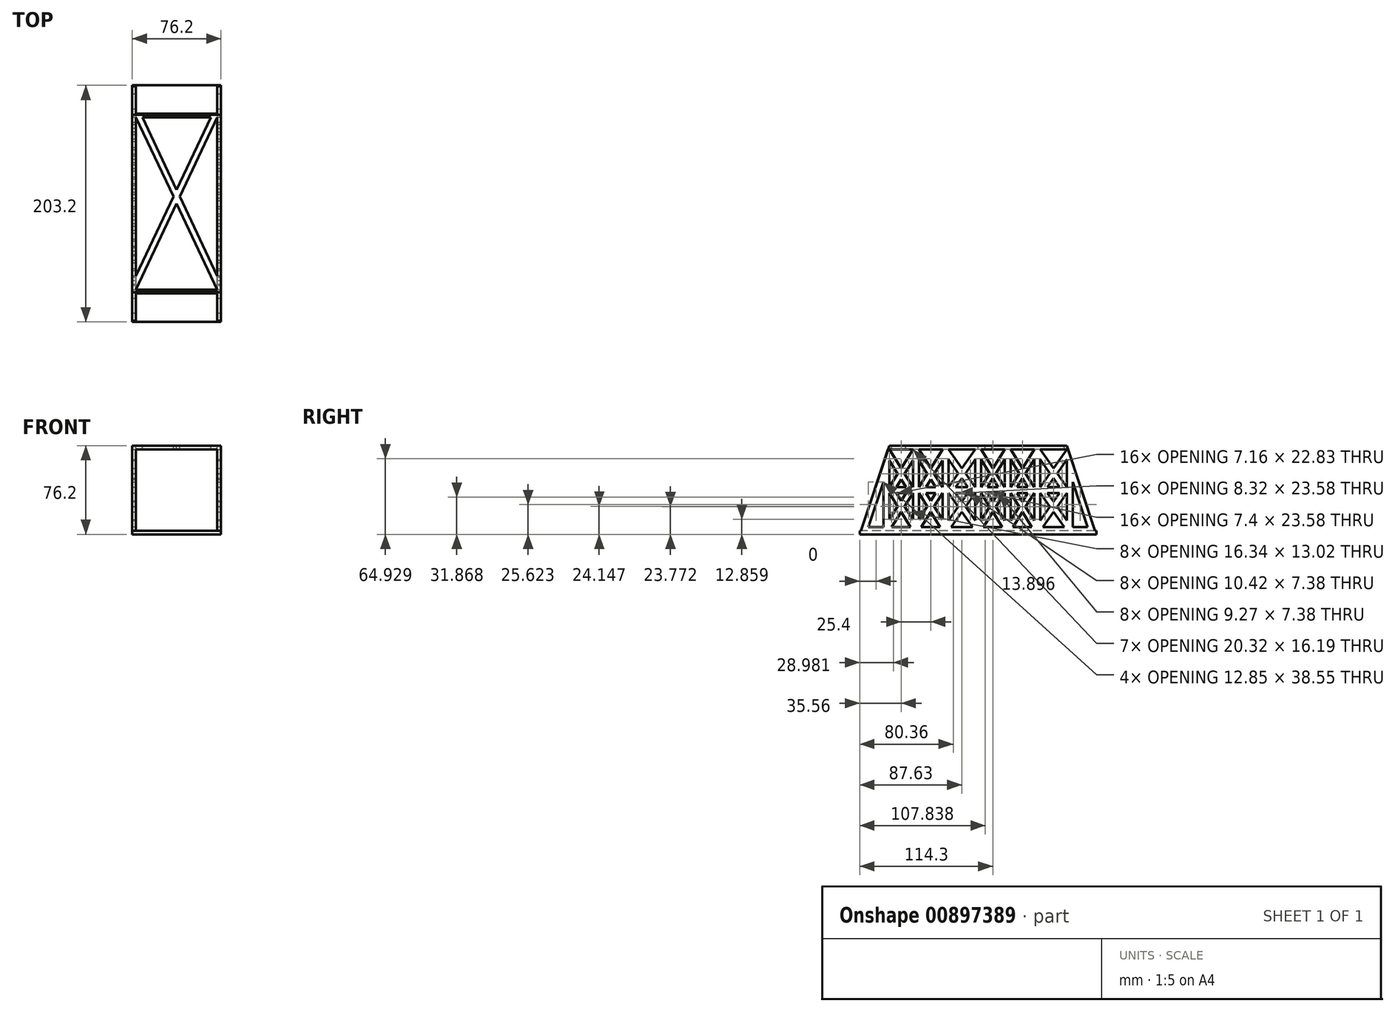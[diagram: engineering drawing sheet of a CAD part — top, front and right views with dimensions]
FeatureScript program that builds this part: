
annotation { "Feature Type Name" : "Feature", "Feature Type Description" : "" }
export const myFeature = defineFeature(function(context is Context, id is Id, definition is map)
    precondition{}
    {
        {
            var Q0;
            Q0=qCreatedBy(makeId("Right.planeOp"),FACE);
            var sketch = newSketch(context, id + "F0", { "sketchPlane" : qUnion([Q0])});
            skLineSegment(sketch, "E0", {"start": v(-101.6, -38.1) * mm, "end": v(101.6, -38.1) * mm});
            skLineSegment(sketch, "E1", {"start": v(-76.2, 38.1) * mm, "end": v(76.2, 38.1) * mm});
            skLineSegment(sketch, "E2", {"start": v(-76.2, 38.1) * mm, "end": v(-101.6, -38.1) * mm});
            skLineSegment(sketch, "E3", {"start": v(76.2, 38.1) * mm, "end": v(101.6, -38.1) * mm});
            skSolve(sketch);
        }
        {
            var Q0;
            Q0 = qSketchRegion(id + "F0", true);
            extrude(context, id + "F1", {"entities" : qUnion([Q0]), "endBound" : BoundingType.SYMMETRIC, "depth" : 76.2 * mm, "offsetDistance" : 25.4 * mm});
        }
        {
            var Q0;
            Q0=makeQuery(id+"F1.opExtrude","CAP_FACE",FACE,{"disambiguationData":[OSD([sQuery(id+"F0.wireOp",EDGE,"E0"),sQuery(id+"F0.wireOp",EDGE,"E1"),sQuery(id+"F0.wireOp",EDGE,"E2"),sQuery(id+"F0.wireOp",EDGE,"E3")])],"isStart":false});
            var sketch = newSketch(context, id + "F2", { "sketchPlane" : qUnion([Q0])});
            skLineSegment(sketch, "E4.bottom", {"start": v(76.2, -34.93) * mm, "end": v(-76.2, -34.93) * mm});
            skLineSegment(sketch, "E4.top", {"start": v(76.2, 34.93) * mm, "end": v(-76.2, 34.93) * mm});
            skLineSegment(sketch, "E4.left", {"start": v(76.2, -34.93) * mm, "end": v(76.2, 34.93) * mm});
            skLineSegment(sketch, "E4.right", {"start": v(-76.2, -34.93) * mm, "end": v(-76.2, 34.93) * mm});
            skPoint(sketch, "E4.middle", {"position": v(0, 0) * mm});
            skLineSegment(sketch, "E5.bottom", {"start": v(76.2, -2.54) * mm, "end": v(-76.2, -2.54) * mm});
            skLineSegment(sketch, "E5.top", {"start": v(76.2, 2.54) * mm, "end": v(-76.2, 2.54) * mm});
            skLineSegment(sketch, "E5.left", {"start": v(76.2, -2.54) * mm, "end": v(76.2, 2.54) * mm});
            skLineSegment(sketch, "E5.right", {"start": v(-76.2, -2.54) * mm, "end": v(-76.2, 2.54) * mm});
            skLineSegment(sketch, "E6.bottom", {"start": v(-50.8, -34.93) * mm, "end": v(-55.88, -34.93) * mm});
            skLineSegment(sketch, "E6.top", {"start": v(-50.8, 34.93) * mm, "end": v(-55.88, 34.93) * mm});
            skLineSegment(sketch, "E6.left", {"start": v(-50.8, -34.92) * mm, "end": v(-50.8, 34.93) * mm});
            skLineSegment(sketch, "E6.right", {"start": v(-55.88, -34.92) * mm, "end": v(-55.88, 34.93) * mm});
            skPoint(sketch, "E6.middle", {"position": v(-53.34, 0) * mm});
            skLineSegment(sketch, "E7.bottom", {"start": v(-25.4, -34.93) * mm, "end": v(-30.48, -34.93) * mm});
            skLineSegment(sketch, "E7.top", {"start": v(-25.4, 34.93) * mm, "end": v(-30.48, 34.93) * mm});
            skLineSegment(sketch, "E7.left", {"start": v(-25.4, -34.93) * mm, "end": v(-25.4, 34.93) * mm});
            skLineSegment(sketch, "E7.right", {"start": v(-30.48, -34.93) * mm, "end": v(-30.48, 34.93) * mm});
            skPoint(sketch, "E7.middle", {"position": v(-27.94, 0) * mm});
            skLineSegment(sketch, "E8.bottom", {"start": v(27.94, -34.93) * mm, "end": v(22.86, -34.93) * mm});
            skLineSegment(sketch, "E8.top", {"start": v(27.94, 34.93) * mm, "end": v(22.86, 34.93) * mm});
            skLineSegment(sketch, "E8.left", {"start": v(27.94, -34.92) * mm, "end": v(27.94, 34.93) * mm});
            skLineSegment(sketch, "E8.right", {"start": v(22.86, -34.93) * mm, "end": v(22.86, 34.93) * mm});
            skPoint(sketch, "E8.middle", {"position": v(25.4, 0) * mm});
            skLineSegment(sketch, "E9.bottom", {"start": v(53.34, -34.93) * mm, "end": v(48.26, -34.93) * mm});
            skLineSegment(sketch, "E9.top", {"start": v(53.34, 34.93) * mm, "end": v(48.26, 34.93) * mm});
            skLineSegment(sketch, "E9.left", {"start": v(53.34, -34.93) * mm, "end": v(53.34, 34.93) * mm});
            skLineSegment(sketch, "E9.right", {"start": v(48.26, -34.93) * mm, "end": v(48.26, 34.93) * mm});
            skPoint(sketch, "E9.middle", {"position": v(50.8, 0) * mm});
            skLineSegment(sketch, "E10.bottom", {"start": v(2.54, -34.93) * mm, "end": v(-2.54, -34.93) * mm});
            skLineSegment(sketch, "E10.top", {"start": v(2.54, 34.93) * mm, "end": v(-2.54, 34.93) * mm});
            skLineSegment(sketch, "E10.left", {"start": v(2.54, -34.93) * mm, "end": v(2.54, 34.93) * mm});
            skLineSegment(sketch, "E10.right", {"start": v(-2.54, -34.93) * mm, "end": v(-2.54, 34.93) * mm});
            skLineSegment(sketch, "E11", {"start": v(-76.2, 34.93) * mm, "end": v(-55.88, 2.54) * mm});
            skLineSegment(sketch, "E12", {"start": v(-55.88, 34.93) * mm, "end": v(-76.2, 2.54) * mm});
            skLineSegment(sketch, "E13", {"start": v(-50.8, 34.93) * mm, "end": v(-30.48, 2.54) * mm});
            skLineSegment(sketch, "E14", {"start": v(-2.54, 34.92) * mm, "end": v(-25.4, 2.54) * mm});
            skLineSegment(sketch, "E15", {"start": v(-76.2, -2.54) * mm, "end": v(-55.88, -34.93) * mm});
            skLineSegment(sketch, "E16", {"start": v(-55.88, -2.54) * mm, "end": v(-76.2, -34.93) * mm});
            skLineSegment(sketch, "E17", {"start": v(-50.8, -2.54) * mm, "end": v(-30.48, -34.92) * mm});
            skLineSegment(sketch, "E18", {"start": v(-30.48, -2.54) * mm, "end": v(-50.8, -34.92) * mm});
            skLineSegment(sketch, "E19", {"start": v(-25.4, -2.54) * mm, "end": v(-2.54, -34.92) * mm});
            skLineSegment(sketch, "E20", {"start": v(-2.54, -2.54) * mm, "end": v(-25.4, -34.93) * mm});
            skLineSegment(sketch, "E21", {"start": v(-55.88, 25.37) * mm, "end": v(-70.2, 2.54) * mm});
            skLineSegment(sketch, "E22", {"start": v(-70.2, -2.54) * mm, "end": v(-55.88, -25.37) * mm});
            skLineSegment(sketch, "E23", {"start": v(-61.88, -2.54) * mm, "end": v(-76.2, -25.37) * mm});
            skLineSegment(sketch, "E24", {"start": v(-44.8, -2.54) * mm, "end": v(-30.48, -25.37) * mm});
            skLineSegment(sketch, "E25", {"start": v(-36.48, -2.54) * mm, "end": v(-50.8, -25.37) * mm});
            skLineSegment(sketch, "E26", {"start": v(-19.18, -2.54) * mm, "end": v(-2.54, -26.12) * mm});
            skLineSegment(sketch, "E27", {"start": v(-8.76, -2.54) * mm, "end": v(-25.4, -26.12) * mm});
            skLineSegment(sketch, "E28", {"start": v(-25.4, 34.93) * mm, "end": v(-2.54, 2.54) * mm});
            skLineSegment(sketch, "E29", {"start": v(-25.4, 26.12) * mm, "end": v(-8.76, 2.54) * mm});
            skLineSegment(sketch, "E30", {"start": v(-2.54, 26.12) * mm, "end": v(-19.18, 2.54) * mm});
            skLineSegment(sketch, "E31", {"start": v(-30.48, 34.92) * mm, "end": v(-50.8, 2.54) * mm});
            skLineSegment(sketch, "E32", {"start": v(-50.8, 25.37) * mm, "end": v(-36.48, 2.54) * mm});
            skLineSegment(sketch, "E33", {"start": v(-30.48, 25.37) * mm, "end": v(-44.8, 2.54) * mm});
            skLineSegment(sketch, "E34", {"start": v(-76.2, 25.37) * mm, "end": v(-61.88, 2.54) * mm});
            skLineSegment(sketch, "E35", {"start": v(2.54, 34.92) * mm, "end": v(22.86, 2.54) * mm});
            skLineSegment(sketch, "E36", {"start": v(22.86, 34.92) * mm, "end": v(2.54, 2.54) * mm});
            skLineSegment(sketch, "E37", {"start": v(2.54, 26.12) * mm, "end": v(17.33, 2.54) * mm});
            skLineSegment(sketch, "E38", {"start": v(22.86, 26.12) * mm, "end": v(8.07, 2.54) * mm});
            skLineSegment(sketch, "E39", {"start": v(27.94, 34.92) * mm, "end": v(48.26, 2.54) * mm});
            skLineSegment(sketch, "E40", {"start": v(27.94, 2.54) * mm, "end": v(48.26, 34.92) * mm});
            skLineSegment(sketch, "E41", {"start": v(53.34, 34.93) * mm, "end": v(76.2, 2.54) * mm});
            skLineSegment(sketch, "E42", {"start": v(53.34, 2.54) * mm, "end": v(76.2, 34.93) * mm});
            skLineSegment(sketch, "E43", {"start": v(53.34, -2.54) * mm, "end": v(76.2, -34.93) * mm});
            skLineSegment(sketch, "E44", {"start": v(53.34, -34.93) * mm, "end": v(76.2, -2.54) * mm});
            skLineSegment(sketch, "E45", {"start": v(48.26, -34.92) * mm, "end": v(27.94, -2.54) * mm});
            skLineSegment(sketch, "E46", {"start": v(48.26, -2.54) * mm, "end": v(27.94, -34.92) * mm});
            skLineSegment(sketch, "E47", {"start": v(2.54, -2.54) * mm, "end": v(22.86, -34.92) * mm});
            skLineSegment(sketch, "E48", {"start": v(22.86, -2.54) * mm, "end": v(2.54, -34.92) * mm});
            skLineSegment(sketch, "E49", {"start": v(27.94, 26.12) * mm, "end": v(42.73, 2.54) * mm});
            skLineSegment(sketch, "E50", {"start": v(48.26, 26.12) * mm, "end": v(33.47, 2.54) * mm});
            skLineSegment(sketch, "E51", {"start": v(53.34, 26.12) * mm, "end": v(69.98, 2.54) * mm});
            skLineSegment(sketch, "E52", {"start": v(76.2, 26.12) * mm, "end": v(59.56, 2.54) * mm});
            skLineSegment(sketch, "E53", {"start": v(59.56, -2.54) * mm, "end": v(76.2, -26.12) * mm});
            skLineSegment(sketch, "E54", {"start": v(69.98, -2.54) * mm, "end": v(53.34, -26.12) * mm});
            skLineSegment(sketch, "E55", {"start": v(48.26, -26.12) * mm, "end": v(33.47, -2.54) * mm});
            skLineSegment(sketch, "E56", {"start": v(42.73, -2.54) * mm, "end": v(27.94, -26.12) * mm});
            skLineSegment(sketch, "E57", {"start": v(22.86, -26.12) * mm, "end": v(8.07, -2.54) * mm});
            skLineSegment(sketch, "E58", {"start": v(17.33, -2.54) * mm, "end": v(2.54, -26.12) * mm});
            skLineSegment(sketch, "E59", {"start": v(-81.28, -34.93) * mm, "end": v(-81.28, 6.8) * mm});
            skLineSegment(sketch, "E60", {"start": v(-81.28, 6.8) * mm, "end": v(-95.19, -34.93) * mm});
            skLineSegment(sketch, "E61", {"start": v(-95.19, -34.92) * mm, "end": v(-81.28, -34.93) * mm});
            skLineSegment(sketch, "E62.MirrorCS", {"start": v(81.28, 6.8) * mm, "end": v(95.19, -34.93) * mm});
            skLineSegment(sketch, "E63.MirrorCS", {"start": v(81.28, -34.93) * mm, "end": v(81.28, 6.8) * mm});
            skLineSegment(sketch, "E64.MirrorCS", {"start": v(95.19, -34.92) * mm, "end": v(81.28, -34.93) * mm});
            skSolve(sketch);
        }
        {
            var Q0;
            Q0=makeQuery(id+"F2.imprint","IMPRINT",FACE,{"disambiguationData":[TD([[makeQuery(id+"F2.imprint","IMPRINT",EDGE,{"derivedFrom":sQuery(id+"F2.wireOp",EDGE,"E59")}),1.0]])]});
            var Q1;
            {var subQ0=sQuery(id+"F2.wireOp",EDGE,"E16");var subQ3=sQuery(id+"F2.wireOp",EDGE,"E15");var subQ5=makeQuery(id+"F2.imprint","INTERSECT",VERTEX,{"derivedFrom":[subQ3,subQ0]});Q1=makeQuery(id+"F2.imprint","IMPRINT",FACE,{"disambiguationData":[TD([[makeQuery(id+"F2.imprint","IMPRINT",EDGE,{"disambiguationData":[TD([[subQ5,-1.0]])],"derivedFrom":subQ0}),1.0]])]});}
            var Q2;
            {var subQ1=sQuery(id+"F2.wireOp",EDGE,"E4.right");var subQ3=sQuery(id+"F2.wireOp",EDGE,"E23");var subQ4=makeQuery(id+"F2.imprint","INTERSECT",VERTEX,{"derivedFrom":[subQ1,subQ3]});Q2=makeQuery(id+"F2.imprint","IMPRINT",FACE,{"disambiguationData":[TD([[makeQuery(id+"F2.imprint","IMPRINT",EDGE,{"disambiguationData":[TD([[subQ4,1.0]])],"derivedFrom":subQ3}),-1.0]])]});}
            var Q3;
            {var subQ0=sQuery(id+"F2.wireOp",EDGE,"E22");var subQ1=sQuery(id+"F2.wireOp",EDGE,"E5.bottom");var subQ2=makeQuery(id+"F2.imprint","INTERSECT",VERTEX,{"derivedFrom":[subQ1,subQ0]});Q3=makeQuery(id+"F2.imprint","IMPRINT",FACE,{"disambiguationData":[TD([[makeQuery(id+"F2.imprint","IMPRINT",EDGE,{"disambiguationData":[TD([[subQ2,1.0]])],"derivedFrom":subQ1}),1.0]])]});}
            var Q4;
            {var subQ1=sQuery(id+"F2.wireOp",EDGE,"E6.right");var subQ3=sQuery(id+"F2.wireOp",EDGE,"E22");var subQ4=makeQuery(id+"F2.imprint","INTERSECT",VERTEX,{"derivedFrom":[subQ1,subQ3]});Q4=makeQuery(id+"F2.imprint","IMPRINT",FACE,{"disambiguationData":[TD([[makeQuery(id+"F2.imprint","IMPRINT",EDGE,{"disambiguationData":[TD([[subQ4,1.0]])],"derivedFrom":subQ3}),1.0]])]});}
            var Q5;
            {var subQ0=sQuery(id+"F2.wireOp",EDGE,"E21");var subQ1=sQuery(id+"F2.wireOp",EDGE,"E5.top");var subQ2=makeQuery(id+"F2.imprint","INTERSECT",VERTEX,{"derivedFrom":[subQ1,subQ0]});Q5=makeQuery(id+"F2.imprint","IMPRINT",FACE,{"disambiguationData":[TD([[makeQuery(id+"F2.imprint","IMPRINT",EDGE,{"disambiguationData":[TD([[subQ2,1.0]])],"derivedFrom":subQ1}),-1.0]])]});}
            var Q6;
            {var subQ0=sQuery(id+"F2.wireOp",EDGE,"E11");var subQ3=sQuery(id+"F2.wireOp",EDGE,"E12");var subQ5=makeQuery(id+"F2.imprint","INTERSECT",VERTEX,{"derivedFrom":[subQ0,subQ3]});Q6=makeQuery(id+"F2.imprint","IMPRINT",FACE,{"disambiguationData":[TD([[makeQuery(id+"F2.imprint","IMPRINT",EDGE,{"disambiguationData":[TD([[subQ5,1.0]])],"derivedFrom":subQ0}),1.0]])]});}
            var Q7;
            {var subQ1=sQuery(id+"F2.wireOp",EDGE,"E4.right");var subQ3=sQuery(id+"F2.wireOp",EDGE,"E34");var subQ4=makeQuery(id+"F2.imprint","INTERSECT",VERTEX,{"derivedFrom":[subQ1,subQ3]});Q7=makeQuery(id+"F2.imprint","IMPRINT",FACE,{"disambiguationData":[TD([[makeQuery(id+"F2.imprint","IMPRINT",EDGE,{"disambiguationData":[TD([[subQ4,-1.0]])],"derivedFrom":subQ3}),-1.0]])]});}
            var Q8;
            {var subQ1=sQuery(id+"F2.wireOp",EDGE,"E6.right");var subQ3=sQuery(id+"F2.wireOp",EDGE,"E21");var subQ4=makeQuery(id+"F2.imprint","INTERSECT",VERTEX,{"derivedFrom":[subQ1,subQ3]});Q8=makeQuery(id+"F2.imprint","IMPRINT",FACE,{"disambiguationData":[TD([[makeQuery(id+"F2.imprint","IMPRINT",EDGE,{"disambiguationData":[TD([[subQ4,-1.0]])],"derivedFrom":subQ3}),1.0]])]});}
            var Q9;
            {var subQ0=sQuery(id+"F2.wireOp",EDGE,"E13");var subQ3=sQuery(id+"F2.wireOp",EDGE,"E31");var subQ5=makeQuery(id+"F2.imprint","INTERSECT",VERTEX,{"derivedFrom":[subQ0,subQ3]});Q9=makeQuery(id+"F2.imprint","IMPRINT",FACE,{"disambiguationData":[TD([[makeQuery(id+"F2.imprint","IMPRINT",EDGE,{"disambiguationData":[TD([[subQ5,1.0]])],"derivedFrom":subQ0}),1.0]])]});}
            var Q10;
            {var subQ1=sQuery(id+"F2.wireOp",EDGE,"E6.left");var subQ3=sQuery(id+"F2.wireOp",EDGE,"E32");var subQ4=makeQuery(id+"F2.imprint","INTERSECT",VERTEX,{"derivedFrom":[subQ1,subQ3]});Q10=makeQuery(id+"F2.imprint","IMPRINT",FACE,{"disambiguationData":[TD([[makeQuery(id+"F2.imprint","IMPRINT",EDGE,{"disambiguationData":[TD([[subQ4,-1.0]])],"derivedFrom":subQ3}),-1.0]])]});}
            var Q11;
            {var subQ1=sQuery(id+"F2.wireOp",EDGE,"E7.right");var subQ3=sQuery(id+"F2.wireOp",EDGE,"E33");var subQ4=makeQuery(id+"F2.imprint","INTERSECT",VERTEX,{"derivedFrom":[subQ1,subQ3]});Q11=makeQuery(id+"F2.imprint","IMPRINT",FACE,{"disambiguationData":[TD([[makeQuery(id+"F2.imprint","IMPRINT",EDGE,{"disambiguationData":[TD([[subQ4,-1.0]])],"derivedFrom":subQ3}),1.0]])]});}
            var Q12;
            {var subQ0=sQuery(id+"F2.wireOp",EDGE,"E32");var subQ1=sQuery(id+"F2.wireOp",EDGE,"E5.top");var subQ2=makeQuery(id+"F2.imprint","INTERSECT",VERTEX,{"derivedFrom":[subQ1,subQ0]});Q12=makeQuery(id+"F2.imprint","IMPRINT",FACE,{"disambiguationData":[TD([[makeQuery(id+"F2.imprint","IMPRINT",EDGE,{"disambiguationData":[TD([[subQ2,-1.0]])],"derivedFrom":subQ1}),-1.0]])]});}
            var Q13;
            {var subQ0=sQuery(id+"F2.wireOp",EDGE,"E24");var subQ1=sQuery(id+"F2.wireOp",EDGE,"E5.bottom");var subQ2=makeQuery(id+"F2.imprint","INTERSECT",VERTEX,{"derivedFrom":[subQ1,subQ0]});Q13=makeQuery(id+"F2.imprint","IMPRINT",FACE,{"disambiguationData":[TD([[makeQuery(id+"F2.imprint","IMPRINT",EDGE,{"disambiguationData":[TD([[subQ2,1.0]])],"derivedFrom":subQ1}),1.0]])]});}
            var Q14;
            {var subQ1=sQuery(id+"F2.wireOp",EDGE,"E6.left");var subQ3=sQuery(id+"F2.wireOp",EDGE,"E25");var subQ4=makeQuery(id+"F2.imprint","INTERSECT",VERTEX,{"derivedFrom":[subQ1,subQ3]});Q14=makeQuery(id+"F2.imprint","IMPRINT",FACE,{"disambiguationData":[TD([[makeQuery(id+"F2.imprint","IMPRINT",EDGE,{"disambiguationData":[TD([[subQ4,1.0]])],"derivedFrom":subQ3}),-1.0]])]});}
            var Q15;
            {var subQ1=sQuery(id+"F2.wireOp",EDGE,"E7.right");var subQ3=sQuery(id+"F2.wireOp",EDGE,"E24");var subQ4=makeQuery(id+"F2.imprint","INTERSECT",VERTEX,{"derivedFrom":[subQ1,subQ3]});Q15=makeQuery(id+"F2.imprint","IMPRINT",FACE,{"disambiguationData":[TD([[makeQuery(id+"F2.imprint","IMPRINT",EDGE,{"disambiguationData":[TD([[subQ4,1.0]])],"derivedFrom":subQ3}),1.0]])]});}
            var Q16;
            {var subQ0=sQuery(id+"F2.wireOp",EDGE,"E18");var subQ3=sQuery(id+"F2.wireOp",EDGE,"E17");var subQ5=makeQuery(id+"F2.imprint","INTERSECT",VERTEX,{"derivedFrom":[subQ3,subQ0]});Q16=makeQuery(id+"F2.imprint","IMPRINT",FACE,{"disambiguationData":[TD([[makeQuery(id+"F2.imprint","IMPRINT",EDGE,{"disambiguationData":[TD([[subQ5,-1.0]])],"derivedFrom":subQ3}),-1.0]])]});}
            var Q17;
            {var subQ1=sQuery(id+"F2.wireOp",EDGE,"E7.left");var subQ3=sQuery(id+"F2.wireOp",EDGE,"E29");var subQ4=makeQuery(id+"F2.imprint","INTERSECT",VERTEX,{"derivedFrom":[subQ1,subQ3]});Q17=makeQuery(id+"F2.imprint","IMPRINT",FACE,{"disambiguationData":[TD([[makeQuery(id+"F2.imprint","IMPRINT",EDGE,{"disambiguationData":[TD([[subQ4,-1.0]])],"derivedFrom":subQ3}),-1.0]])]});}
            var Q18;
            {var subQ0=sQuery(id+"F2.wireOp",EDGE,"E28");var subQ3=sQuery(id+"F2.wireOp",EDGE,"E14");var subQ5=makeQuery(id+"F2.imprint","INTERSECT",VERTEX,{"derivedFrom":[subQ3,subQ0]});Q18=makeQuery(id+"F2.imprint","IMPRINT",FACE,{"disambiguationData":[TD([[makeQuery(id+"F2.imprint","IMPRINT",EDGE,{"disambiguationData":[TD([[subQ5,1.0]])],"derivedFrom":subQ3}),-1.0]])]});}
            var Q19;
            {var subQ1=sQuery(id+"F2.wireOp",EDGE,"E10.right");var subQ3=sQuery(id+"F2.wireOp",EDGE,"E30");var subQ4=makeQuery(id+"F2.imprint","INTERSECT",VERTEX,{"derivedFrom":[subQ1,subQ3]});Q19=makeQuery(id+"F2.imprint","IMPRINT",FACE,{"disambiguationData":[TD([[makeQuery(id+"F2.imprint","IMPRINT",EDGE,{"disambiguationData":[TD([[subQ4,-1.0]])],"derivedFrom":subQ3}),1.0]])]});}
            var Q20;
            {var subQ0=sQuery(id+"F2.wireOp",EDGE,"E29");var subQ1=sQuery(id+"F2.wireOp",EDGE,"E5.top");var subQ2=makeQuery(id+"F2.imprint","INTERSECT",VERTEX,{"derivedFrom":[subQ1,subQ0]});Q20=makeQuery(id+"F2.imprint","IMPRINT",FACE,{"disambiguationData":[TD([[makeQuery(id+"F2.imprint","IMPRINT",EDGE,{"disambiguationData":[TD([[subQ2,-1.0]])],"derivedFrom":subQ1}),-1.0]])]});}
            var Q21;
            {var subQ0=sQuery(id+"F2.wireOp",EDGE,"E26");var subQ1=sQuery(id+"F2.wireOp",EDGE,"E5.bottom");var subQ2=makeQuery(id+"F2.imprint","INTERSECT",VERTEX,{"derivedFrom":[subQ1,subQ0]});Q21=makeQuery(id+"F2.imprint","IMPRINT",FACE,{"disambiguationData":[TD([[makeQuery(id+"F2.imprint","IMPRINT",EDGE,{"disambiguationData":[TD([[subQ2,1.0]])],"derivedFrom":subQ1}),1.0]])]});}
            var Q22;
            {var subQ1=sQuery(id+"F2.wireOp",EDGE,"E7.left");var subQ3=sQuery(id+"F2.wireOp",EDGE,"E27");var subQ4=makeQuery(id+"F2.imprint","INTERSECT",VERTEX,{"derivedFrom":[subQ1,subQ3]});Q22=makeQuery(id+"F2.imprint","IMPRINT",FACE,{"disambiguationData":[TD([[makeQuery(id+"F2.imprint","IMPRINT",EDGE,{"disambiguationData":[TD([[subQ4,1.0]])],"derivedFrom":subQ3}),-1.0]])]});}
            var Q23;
            {var subQ1=sQuery(id+"F2.wireOp",EDGE,"E10.right");var subQ3=sQuery(id+"F2.wireOp",EDGE,"E26");var subQ4=makeQuery(id+"F2.imprint","INTERSECT",VERTEX,{"derivedFrom":[subQ1,subQ3]});Q23=makeQuery(id+"F2.imprint","IMPRINT",FACE,{"disambiguationData":[TD([[makeQuery(id+"F2.imprint","IMPRINT",EDGE,{"disambiguationData":[TD([[subQ4,1.0]])],"derivedFrom":subQ3}),1.0]])]});}
            var Q24;
            {var subQ0=sQuery(id+"F2.wireOp",EDGE,"E20");var subQ3=sQuery(id+"F2.wireOp",EDGE,"E19");var subQ5=makeQuery(id+"F2.imprint","INTERSECT",VERTEX,{"derivedFrom":[subQ3,subQ0]});Q24=makeQuery(id+"F2.imprint","IMPRINT",FACE,{"disambiguationData":[TD([[makeQuery(id+"F2.imprint","IMPRINT",EDGE,{"disambiguationData":[TD([[subQ5,-1.0]])],"derivedFrom":subQ3}),-1.0]])]});}
            var Q25;
            {var subQ1=sQuery(id+"F2.wireOp",EDGE,"E10.left");var subQ3=sQuery(id+"F2.wireOp",EDGE,"E37");var subQ4=makeQuery(id+"F2.imprint","INTERSECT",VERTEX,{"derivedFrom":[subQ1,subQ3]});Q25=makeQuery(id+"F2.imprint","IMPRINT",FACE,{"disambiguationData":[TD([[makeQuery(id+"F2.imprint","IMPRINT",EDGE,{"disambiguationData":[TD([[subQ4,-1.0]])],"derivedFrom":subQ3}),-1.0]])]});}
            var Q26;
            {var subQ0=sQuery(id+"F2.wireOp",EDGE,"E36");var subQ3=sQuery(id+"F2.wireOp",EDGE,"E35");var subQ5=makeQuery(id+"F2.imprint","INTERSECT",VERTEX,{"derivedFrom":[subQ3,subQ0]});Q26=makeQuery(id+"F2.imprint","IMPRINT",FACE,{"disambiguationData":[TD([[makeQuery(id+"F2.imprint","IMPRINT",EDGE,{"disambiguationData":[TD([[subQ5,1.0]])],"derivedFrom":subQ3}),1.0]])]});}
            var Q27;
            {var subQ1=sQuery(id+"F2.wireOp",EDGE,"E8.right");var subQ3=sQuery(id+"F2.wireOp",EDGE,"E38");var subQ4=makeQuery(id+"F2.imprint","INTERSECT",VERTEX,{"derivedFrom":[subQ1,subQ3]});Q27=makeQuery(id+"F2.imprint","IMPRINT",FACE,{"disambiguationData":[TD([[makeQuery(id+"F2.imprint","IMPRINT",EDGE,{"disambiguationData":[TD([[subQ4,-1.0]])],"derivedFrom":subQ3}),1.0]])]});}
            var Q28;
            {var subQ0=sQuery(id+"F2.wireOp",EDGE,"E37");var subQ1=sQuery(id+"F2.wireOp",EDGE,"E5.top");var subQ2=makeQuery(id+"F2.imprint","INTERSECT",VERTEX,{"derivedFrom":[subQ1,subQ0]});Q28=makeQuery(id+"F2.imprint","IMPRINT",FACE,{"disambiguationData":[TD([[makeQuery(id+"F2.imprint","IMPRINT",EDGE,{"disambiguationData":[TD([[subQ2,-1.0]])],"derivedFrom":subQ1}),-1.0]])]});}
            var Q29;
            {var subQ0=sQuery(id+"F2.wireOp",EDGE,"E57");var subQ1=sQuery(id+"F2.wireOp",EDGE,"E5.bottom");var subQ2=makeQuery(id+"F2.imprint","INTERSECT",VERTEX,{"derivedFrom":[subQ1,subQ0]});Q29=makeQuery(id+"F2.imprint","IMPRINT",FACE,{"disambiguationData":[TD([[makeQuery(id+"F2.imprint","IMPRINT",EDGE,{"disambiguationData":[TD([[subQ2,1.0]])],"derivedFrom":subQ1}),1.0]])]});}
            var Q30;
            {var subQ1=sQuery(id+"F2.wireOp",EDGE,"E10.left");var subQ3=sQuery(id+"F2.wireOp",EDGE,"E58");var subQ4=makeQuery(id+"F2.imprint","INTERSECT",VERTEX,{"derivedFrom":[subQ1,subQ3]});Q30=makeQuery(id+"F2.imprint","IMPRINT",FACE,{"disambiguationData":[TD([[makeQuery(id+"F2.imprint","IMPRINT",EDGE,{"disambiguationData":[TD([[subQ4,1.0]])],"derivedFrom":subQ3}),-1.0]])]});}
            var Q31;
            {var subQ1=sQuery(id+"F2.wireOp",EDGE,"E8.right");var subQ3=sQuery(id+"F2.wireOp",EDGE,"E57");var subQ4=makeQuery(id+"F2.imprint","INTERSECT",VERTEX,{"derivedFrom":[subQ1,subQ3]});Q31=makeQuery(id+"F2.imprint","IMPRINT",FACE,{"disambiguationData":[TD([[makeQuery(id+"F2.imprint","IMPRINT",EDGE,{"disambiguationData":[TD([[subQ4,-1.0]])],"derivedFrom":subQ3}),-1.0]])]});}
            var Q32;
            {var subQ0=sQuery(id+"F2.wireOp",EDGE,"E47");var subQ3=sQuery(id+"F2.wireOp",EDGE,"E48");var subQ5=makeQuery(id+"F2.imprint","INTERSECT",VERTEX,{"derivedFrom":[subQ0,subQ3]});Q32=makeQuery(id+"F2.imprint","IMPRINT",FACE,{"disambiguationData":[TD([[makeQuery(id+"F2.imprint","IMPRINT",EDGE,{"disambiguationData":[TD([[subQ5,-1.0]])],"derivedFrom":subQ0}),-1.0]])]});}
            var Q33;
            {var subQ1=sQuery(id+"F2.wireOp",EDGE,"E8.left");var subQ3=sQuery(id+"F2.wireOp",EDGE,"E49");var subQ4=makeQuery(id+"F2.imprint","INTERSECT",VERTEX,{"derivedFrom":[subQ1,subQ3]});Q33=makeQuery(id+"F2.imprint","IMPRINT",FACE,{"disambiguationData":[TD([[makeQuery(id+"F2.imprint","IMPRINT",EDGE,{"disambiguationData":[TD([[subQ4,-1.0]])],"derivedFrom":subQ3}),-1.0]])]});}
            var Q34;
            {var subQ0=sQuery(id+"F2.wireOp",EDGE,"E39");var subQ3=sQuery(id+"F2.wireOp",EDGE,"E40");var subQ5=makeQuery(id+"F2.imprint","INTERSECT",VERTEX,{"derivedFrom":[subQ0,subQ3]});Q34=makeQuery(id+"F2.imprint","IMPRINT",FACE,{"disambiguationData":[TD([[makeQuery(id+"F2.imprint","IMPRINT",EDGE,{"disambiguationData":[TD([[subQ5,1.0]])],"derivedFrom":subQ0}),1.0]])]});}
            var Q35;
            {var subQ1=sQuery(id+"F2.wireOp",EDGE,"E9.right");var subQ3=sQuery(id+"F2.wireOp",EDGE,"E50");var subQ4=makeQuery(id+"F2.imprint","INTERSECT",VERTEX,{"derivedFrom":[subQ1,subQ3]});Q35=makeQuery(id+"F2.imprint","IMPRINT",FACE,{"disambiguationData":[TD([[makeQuery(id+"F2.imprint","IMPRINT",EDGE,{"disambiguationData":[TD([[subQ4,-1.0]])],"derivedFrom":subQ3}),1.0]])]});}
            var Q36;
            {var subQ0=sQuery(id+"F2.wireOp",EDGE,"E49");var subQ1=sQuery(id+"F2.wireOp",EDGE,"E5.top");var subQ2=makeQuery(id+"F2.imprint","INTERSECT",VERTEX,{"derivedFrom":[subQ1,subQ0]});Q36=makeQuery(id+"F2.imprint","IMPRINT",FACE,{"disambiguationData":[TD([[makeQuery(id+"F2.imprint","IMPRINT",EDGE,{"disambiguationData":[TD([[subQ2,-1.0]])],"derivedFrom":subQ1}),-1.0]])]});}
            var Q37;
            {var subQ0=sQuery(id+"F2.wireOp",EDGE,"E55");var subQ1=sQuery(id+"F2.wireOp",EDGE,"E5.bottom");var subQ2=makeQuery(id+"F2.imprint","INTERSECT",VERTEX,{"derivedFrom":[subQ1,subQ0]});Q37=makeQuery(id+"F2.imprint","IMPRINT",FACE,{"disambiguationData":[TD([[makeQuery(id+"F2.imprint","IMPRINT",EDGE,{"disambiguationData":[TD([[subQ2,1.0]])],"derivedFrom":subQ1}),1.0]])]});}
            var Q38;
            {var subQ1=sQuery(id+"F2.wireOp",EDGE,"E8.left");var subQ3=sQuery(id+"F2.wireOp",EDGE,"E56");var subQ4=makeQuery(id+"F2.imprint","INTERSECT",VERTEX,{"derivedFrom":[subQ1,subQ3]});Q38=makeQuery(id+"F2.imprint","IMPRINT",FACE,{"disambiguationData":[TD([[makeQuery(id+"F2.imprint","IMPRINT",EDGE,{"disambiguationData":[TD([[subQ4,1.0]])],"derivedFrom":subQ3}),-1.0]])]});}
            var Q39;
            {var subQ1=sQuery(id+"F2.wireOp",EDGE,"E9.right");var subQ3=sQuery(id+"F2.wireOp",EDGE,"E55");var subQ4=makeQuery(id+"F2.imprint","INTERSECT",VERTEX,{"derivedFrom":[subQ1,subQ3]});Q39=makeQuery(id+"F2.imprint","IMPRINT",FACE,{"disambiguationData":[TD([[makeQuery(id+"F2.imprint","IMPRINT",EDGE,{"disambiguationData":[TD([[subQ4,-1.0]])],"derivedFrom":subQ3}),-1.0]])]});}
            var Q40;
            {var subQ0=sQuery(id+"F2.wireOp",EDGE,"E46");var subQ3=sQuery(id+"F2.wireOp",EDGE,"E45");var subQ5=makeQuery(id+"F2.imprint","INTERSECT",VERTEX,{"derivedFrom":[subQ3,subQ0]});Q40=makeQuery(id+"F2.imprint","IMPRINT",FACE,{"disambiguationData":[TD([[makeQuery(id+"F2.imprint","IMPRINT",EDGE,{"disambiguationData":[TD([[subQ5,1.0]])],"derivedFrom":subQ3}),1.0]])]});}
            var Q41;
            {var subQ1=sQuery(id+"F2.wireOp",EDGE,"E9.left");var subQ3=sQuery(id+"F2.wireOp",EDGE,"E51");var subQ4=makeQuery(id+"F2.imprint","INTERSECT",VERTEX,{"derivedFrom":[subQ1,subQ3]});Q41=makeQuery(id+"F2.imprint","IMPRINT",FACE,{"disambiguationData":[TD([[makeQuery(id+"F2.imprint","IMPRINT",EDGE,{"disambiguationData":[TD([[subQ4,-1.0]])],"derivedFrom":subQ3}),-1.0]])]});}
            var Q42;
            {var subQ0=sQuery(id+"F2.wireOp",EDGE,"E42");var subQ3=sQuery(id+"F2.wireOp",EDGE,"E41");var subQ5=makeQuery(id+"F2.imprint","INTERSECT",VERTEX,{"derivedFrom":[subQ3,subQ0]});Q42=makeQuery(id+"F2.imprint","IMPRINT",FACE,{"disambiguationData":[TD([[makeQuery(id+"F2.imprint","IMPRINT",EDGE,{"disambiguationData":[TD([[subQ5,-1.0]])],"derivedFrom":subQ0}),1.0]])]});}
            var Q43;
            {var subQ1=sQuery(id+"F2.wireOp",EDGE,"E4.left");var subQ3=sQuery(id+"F2.wireOp",EDGE,"E52");var subQ4=makeQuery(id+"F2.imprint","INTERSECT",VERTEX,{"derivedFrom":[subQ1,subQ3]});Q43=makeQuery(id+"F2.imprint","IMPRINT",FACE,{"disambiguationData":[TD([[makeQuery(id+"F2.imprint","IMPRINT",EDGE,{"disambiguationData":[TD([[subQ4,-1.0]])],"derivedFrom":subQ3}),1.0]])]});}
            var Q44;
            {var subQ0=sQuery(id+"F2.wireOp",EDGE,"E51");var subQ1=sQuery(id+"F2.wireOp",EDGE,"E5.top");var subQ2=makeQuery(id+"F2.imprint","INTERSECT",VERTEX,{"derivedFrom":[subQ1,subQ0]});Q44=makeQuery(id+"F2.imprint","IMPRINT",FACE,{"disambiguationData":[TD([[makeQuery(id+"F2.imprint","IMPRINT",EDGE,{"disambiguationData":[TD([[subQ2,-1.0]])],"derivedFrom":subQ1}),-1.0]])]});}
            var Q45;
            {var subQ0=sQuery(id+"F2.wireOp",EDGE,"E53");var subQ1=sQuery(id+"F2.wireOp",EDGE,"E5.bottom");var subQ2=makeQuery(id+"F2.imprint","INTERSECT",VERTEX,{"derivedFrom":[subQ1,subQ0]});Q45=makeQuery(id+"F2.imprint","IMPRINT",FACE,{"disambiguationData":[TD([[makeQuery(id+"F2.imprint","IMPRINT",EDGE,{"disambiguationData":[TD([[subQ2,1.0]])],"derivedFrom":subQ1}),1.0]])]});}
            var Q46;
            {var subQ1=sQuery(id+"F2.wireOp",EDGE,"E9.left");var subQ3=sQuery(id+"F2.wireOp",EDGE,"E54");var subQ4=makeQuery(id+"F2.imprint","INTERSECT",VERTEX,{"derivedFrom":[subQ1,subQ3]});Q46=makeQuery(id+"F2.imprint","IMPRINT",FACE,{"disambiguationData":[TD([[makeQuery(id+"F2.imprint","IMPRINT",EDGE,{"disambiguationData":[TD([[subQ4,1.0]])],"derivedFrom":subQ3}),-1.0]])]});}
            var Q47;
            {var subQ0=sQuery(id+"F2.wireOp",EDGE,"E43");var subQ3=sQuery(id+"F2.wireOp",EDGE,"E44");var subQ5=makeQuery(id+"F2.imprint","INTERSECT",VERTEX,{"derivedFrom":[subQ0,subQ3]});Q47=makeQuery(id+"F2.imprint","IMPRINT",FACE,{"disambiguationData":[TD([[makeQuery(id+"F2.imprint","IMPRINT",EDGE,{"disambiguationData":[TD([[subQ5,-1.0]])],"derivedFrom":subQ0}),-1.0]])]});}
            var Q48;
            {var subQ1=sQuery(id+"F2.wireOp",EDGE,"E4.left");var subQ3=sQuery(id+"F2.wireOp",EDGE,"E53");var subQ4=makeQuery(id+"F2.imprint","INTERSECT",VERTEX,{"derivedFrom":[subQ1,subQ3]});Q48=makeQuery(id+"F2.imprint","IMPRINT",FACE,{"disambiguationData":[TD([[makeQuery(id+"F2.imprint","IMPRINT",EDGE,{"disambiguationData":[TD([[subQ4,1.0]])],"derivedFrom":subQ3}),1.0]])]});}
            var Q49;
            Q49=makeQuery(id+"F2.imprint","IMPRINT",FACE,{"disambiguationData":[TD([[makeQuery(id+"F2.imprint","IMPRINT",EDGE,{"derivedFrom":sQuery(id+"F2.wireOp",EDGE,"E62.MirrorCS")}),-1.0]])]});
            extrude(context, id + "F3", {"entities" : qUnion([Q0, Q1, Q2, Q3, Q4, Q5, Q6, Q7, Q8, Q9, Q10, Q11, Q12, Q13, Q14, Q15, Q16, Q17, Q18, Q19, Q20, Q21, Q22, Q23, Q24, Q25, Q26, Q27, Q28, Q29, Q30, Q31, Q32, Q33, Q34, Q35, Q36, Q37, Q38, Q39, Q40, Q41, Q42, Q43, Q44, Q45, Q46, Q47, Q48, Q49]), "operationType" : NewBodyOperationType.REMOVE, "oppositeDirection" : true, "depth" : 76.2 * mm, "offsetDistance" : 25.4 * mm});
        }
        {
            var Q0;
            Q0=qCreatedBy(makeId("Front.planeOp"),FACE);
            var sketch = newSketch(context, id + "F4", { "sketchPlane" : qUnion([Q0])});
            skLineSegment(sketch, "E65.bottom", {"start": v(34.92, -34.93) * mm, "end": v(-34.92, -34.93) * mm});
            skLineSegment(sketch, "E65.top", {"start": v(34.92, 34.93) * mm, "end": v(-34.92, 34.93) * mm});
            skLineSegment(sketch, "E65.left", {"start": v(34.92, -34.93) * mm, "end": v(34.92, 34.93) * mm});
            skLineSegment(sketch, "E65.right", {"start": v(-34.92, -34.93) * mm, "end": v(-34.92, 34.93) * mm});
            skPoint(sketch, "E65.middle", {"position": v(0, 0) * mm});
            skSolve(sketch);
        }
        {
            var Q0;
            Q0 = qSketchRegion(id + "F4", true);
            extrude(context, id + "F5", {"entities" : qUnion([Q0]), "operationType" : NewBodyOperationType.REMOVE, "endBound" : BoundingType.SYMMETRIC, "oppositeDirection" : true, "depth" : 254 * mm, "offsetDistance" : 25.4 * mm});
        }
        {
            var Q0;
            Q0=makeQuery(id+"F1.opExtrude","SWEPT_FACE",FACE,{"disambiguationData":[OSD([sQuery(id+"F0.wireOp",EDGE,"E1")])]});
            var sketch = newSketch(context, id + "F6", { "sketchPlane" : qUnion([Q0])});
            skLineSegment(sketch, "E66.bottom", {"start": v(34.93, -74.08) * mm, "end": v(-34.93, -74.08) * mm});
            skLineSegment(sketch, "E66.top", {"start": v(34.93, 74.08) * mm, "end": v(-34.93, 74.08) * mm});
            skLineSegment(sketch, "E66.left", {"start": v(34.93, -74.08) * mm, "end": v(34.93, 74.08) * mm});
            skLineSegment(sketch, "E66.right", {"start": v(-34.93, -74.08) * mm, "end": v(-34.93, 74.08) * mm});
            skPoint(sketch, "E66.middle", {"position": v(0, 0) * mm});
            skLineSegment(sketch, "E67", {"start": v(-34.93, 74.08) * mm, "end": v(34.93, -74.08) * mm});
            skLineSegment(sketch, "E68", {"start": v(34.92, 74.08) * mm, "end": v(-34.92, -74.08) * mm});
            skLineSegment(sketch, "E69", {"start": v(-29.3, 74.08) * mm, "end": v(34.93, -62.17) * mm});
            skLineSegment(sketch, "E70", {"start": v(29.3, 74.08) * mm, "end": v(-34.93, -62.17) * mm});
            skSolve(sketch);
        }
        {
            var Q0;
            {var subQ1=sQuery(id+"F6.wireOp",EDGE,"E66.right");var subQ3=sQuery(id+"F6.wireOp",EDGE,"E70");var subQ4=makeQuery(id+"F6.imprint","INTERSECT",VERTEX,{"derivedFrom":[subQ1,subQ3]});Q0=makeQuery(id+"F6.imprint","IMPRINT",FACE,{"disambiguationData":[TD([[makeQuery(id+"F6.imprint","IMPRINT",EDGE,{"disambiguationData":[TD([[subQ4,1.0]])],"derivedFrom":subQ3}),-1.0]])]});}
            var Q1;
            {var subQ0=sQuery(id+"F6.wireOp",EDGE,"E69");var subQ1=sQuery(id+"F6.wireOp",EDGE,"E66.top");var subQ2=makeQuery(id+"F6.imprint","INTERSECT",VERTEX,{"derivedFrom":[subQ1,subQ0]});Q1=makeQuery(id+"F6.imprint","IMPRINT",FACE,{"disambiguationData":[TD([[makeQuery(id+"F6.imprint","IMPRINT",EDGE,{"disambiguationData":[TD([[subQ2,1.0]])],"derivedFrom":subQ1}),1.0]])]});}
            var Q2;
            {var subQ1=sQuery(id+"F6.wireOp",EDGE,"E66.left");var subQ3=sQuery(id+"F6.wireOp",EDGE,"E69");var subQ4=makeQuery(id+"F6.imprint","INTERSECT",VERTEX,{"derivedFrom":[subQ1,subQ3]});Q2=makeQuery(id+"F6.imprint","IMPRINT",FACE,{"disambiguationData":[TD([[makeQuery(id+"F6.imprint","IMPRINT",EDGE,{"disambiguationData":[TD([[subQ4,1.0]])],"derivedFrom":subQ3}),1.0]])]});}
            var Q3;
            {var subQ0=sQuery(id+"F6.wireOp",EDGE,"E66.bottom");Q3=makeQuery(id+"F6.imprint","IMPRINT",FACE,{"disambiguationData":[TD([[makeQuery(id+"F6.imprint","IMPRINT",EDGE,{"derivedFrom":subQ0}),-1.0]])]});}
            extrude(context, id + "F7", {"entities" : qUnion([Q0, Q1, Q2, Q3]), "operationType" : NewBodyOperationType.REMOVE, "oppositeDirection" : true, "depth" : 3.17 * mm, "offsetDistance" : 25.4 * mm});
        }
        {
            var Q0;
            Q0=makeQuery(id+"F1.opExtrude","CAP_FACE",FACE,{"disambiguationData":[OSD([sQuery(id+"F0.wireOp",EDGE,"E0"),sQuery(id+"F0.wireOp",EDGE,"E1"),sQuery(id+"F0.wireOp",EDGE,"E2"),sQuery(id+"F0.wireOp",EDGE,"E3")])],"isStart":false});
            var sketch = newSketch(context, id + "F8", { "sketchPlane" : qUnion([Q0])});
            skLineSegment(sketch, "E71.bottom", {"start": v(-101.6, -38.1) * mm, "end": v(-95.19, -38.1) * mm});
            skLineSegment(sketch, "E71.top", {"start": v(-101.6, -34.93) * mm, "end": v(-95.19, -34.93) * mm});
            skLineSegment(sketch, "E71.left", {"start": v(-101.6, -38.1) * mm, "end": v(-101.6, -34.93) * mm});
            skLineSegment(sketch, "E71.right", {"start": v(-95.19, -38.1) * mm, "end": v(-95.19, -34.93) * mm});
            skLineSegment(sketch, "E72.MirrorCS", {"start": v(101.6, -38.1) * mm, "end": v(95.19, -38.1) * mm});
            skLineSegment(sketch, "E73.MirrorCS", {"start": v(101.6, -34.93) * mm, "end": v(95.19, -34.93) * mm});
            skLineSegment(sketch, "E74.MirrorCS", {"start": v(101.6, -38.1) * mm, "end": v(101.6, -34.93) * mm});
            skLineSegment(sketch, "E75.MirrorCS", {"start": v(95.19, -38.1) * mm, "end": v(95.19, -34.93) * mm});
            skSolve(sketch);
        }
        {
            var Q0;
            Q0 = qSketchRegion(id + "F8", true);
            extrude(context, id + "F9", {"entities" : qUnion([Q0]), "operationType" : NewBodyOperationType.ADD, "oppositeDirection" : true, "depth" : 76.2 * mm, "offsetDistance" : 25.4 * mm});
        }
        {
            var Q0;
            {var subQ0=sQuery(id+"F2.wireOp",EDGE,"E4.bottom");var subQ1=sQuery(id+"F2.wireOp",EDGE,"E6.bottom");var subQ2=sQuery(id+"F2.wireOp",EDGE,"E7.bottom");var subQ4=sQuery(id+"F2.wireOp",EDGE,"E8.bottom");Q0=makeQuery(id+"F9.boolean.opBoolean","MERGE",FACE,{"derivedFrom":[makeQuery(id+"F5.boolean.opBoolean","MERGE",FACE,{"derivedFrom":[makeQuery(id+"F3.boolean.opBoolean","COPY",FACE,{"derivedFrom":makeQuery(id+"F3.opExtrude","SWEPT_FACE",FACE,{"disambiguationData":[OSD([subQ0]),TDD([makeQuery(id+"F2.imprint","IMPRINT",EDGE,{"disambiguationData":[TD([[makeQuery(id+"F2.imprint","INTERSECT",VERTEX,{"derivedFrom":[subQ0,sQuery(id+"F2.wireOp",EDGE,"E4.left"),sQuery(id+"F2.wireOp",EDGE,"E43")]}),-1.0]])],"derivedFrom":subQ0})])]})}),makeQuery(id+"F3.boolean.opBoolean","COPY",FACE,{"derivedFrom":makeQuery(id+"F3.opExtrude","SWEPT_FACE",FACE,{"disambiguationData":[OSD([subQ0]),TDD([makeQuery(id+"F2.imprint","IMPRINT",EDGE,{"disambiguationData":[TD([[makeQuery(id+"F2.imprint","INTERSECT",VERTEX,{"derivedFrom":[subQ0,subQ4,sQuery(id+"F2.wireOp",EDGE,"E8.left"),sQuery(id+"F2.wireOp",EDGE,"E46")]}),1.0]])],"derivedFrom":subQ0})])]})}),makeQuery(id+"F3.boolean.opBoolean","COPY",FACE,{"derivedFrom":makeQuery(id+"F3.opExtrude","SWEPT_FACE",FACE,{"disambiguationData":[OSD([subQ0]),TDD([makeQuery(id+"F2.imprint","IMPRINT",EDGE,{"disambiguationData":[TD([[makeQuery(id+"F2.imprint","INTERSECT",VERTEX,{"derivedFrom":[subQ0,subQ4,sQuery(id+"F2.wireOp",EDGE,"E8.right"),sQuery(id+"F2.wireOp",EDGE,"E47")]}),-1.0]])],"derivedFrom":subQ0})])]})}),makeQuery(id+"F3.boolean.opBoolean","COPY",FACE,{"derivedFrom":makeQuery(id+"F3.opExtrude","SWEPT_FACE",FACE,{"disambiguationData":[OSD([subQ0]),TDD([makeQuery(id+"F2.imprint","IMPRINT",EDGE,{"disambiguationData":[TD([[makeQuery(id+"F2.imprint","INTERSECT",VERTEX,{"derivedFrom":[subQ0,subQ2,sQuery(id+"F2.wireOp",EDGE,"E7.left"),sQuery(id+"F2.wireOp",EDGE,"E20")]}),1.0]])],"derivedFrom":subQ0})])]})}),makeQuery(id+"F3.boolean.opBoolean","COPY",FACE,{"derivedFrom":makeQuery(id+"F3.opExtrude","SWEPT_FACE",FACE,{"disambiguationData":[OSD([subQ0]),TDD([makeQuery(id+"F2.imprint","IMPRINT",EDGE,{"disambiguationData":[TD([[makeQuery(id+"F2.imprint","INTERSECT",VERTEX,{"derivedFrom":[subQ0,subQ1,sQuery(id+"F2.wireOp",EDGE,"E6.left"),sQuery(id+"F2.wireOp",EDGE,"E18")]}),1.0]])],"derivedFrom":subQ0})])]})}),makeQuery(id+"F3.boolean.opBoolean","COPY",FACE,{"derivedFrom":makeQuery(id+"F3.opExtrude","SWEPT_FACE",FACE,{"disambiguationData":[OSD([subQ0]),TDD([makeQuery(id+"F2.imprint","IMPRINT",EDGE,{"disambiguationData":[TD([[makeQuery(id+"F2.imprint","INTERSECT",VERTEX,{"derivedFrom":[subQ0,sQuery(id+"F2.wireOp",EDGE,"E4.right"),sQuery(id+"F2.wireOp",EDGE,"E16")]}),1.0]])],"derivedFrom":subQ0})])]})}),makeQuery(id+"F3.boolean.opBoolean","COPY",FACE,{"derivedFrom":makeQuery(id+"F3.opExtrude","SWEPT_FACE",FACE,{"disambiguationData":[OSD([sQuery(id+"F2.wireOp",EDGE,"E61")])]})}),makeQuery(id+"F3.boolean.opBoolean","COPY",FACE,{"derivedFrom":makeQuery(id+"F3.opExtrude","SWEPT_FACE",FACE,{"disambiguationData":[OSD([sQuery(id+"F2.wireOp",EDGE,"E64.MirrorCS")])]})})],"fromTools":[makeQuery(id+"F5.opExtrude","SWEPT_FACE",FACE,{"disambiguationData":[OSD([sQuery(id+"F4.wireOp",EDGE,"E65.bottom")])]})]}),makeQuery(id+"F9.opExtrude","SWEPT_FACE",FACE,{"disambiguationData":[OSD([sQuery(id+"F8.wireOp",EDGE,"E71.top")])]}),makeQuery(id+"F9.opExtrude","SWEPT_FACE",FACE,{"disambiguationData":[OSD([sQuery(id+"F8.wireOp",EDGE,"E73.MirrorCS")])]})]});}
            var sketch = newSketch(context, id + "F10", { "sketchPlane" : qUnion([Q0])});
            skLineSegment(sketch, "E76.bottom", {"start": v(38.1, -95.19) * mm, "end": v(34.92, -95.19) * mm});
            skLineSegment(sketch, "E76.top", {"start": v(38.1, 95.19) * mm, "end": v(34.92, 95.19) * mm});
            skLineSegment(sketch, "E76.left", {"start": v(38.1, -95.19) * mm, "end": v(38.1, 95.19) * mm});
            skLineSegment(sketch, "E76.right", {"start": v(34.92, -95.19) * mm, "end": v(34.92, 95.19) * mm});
            skLineSegment(sketch, "E77.MirrorCS", {"start": v(-38.1, -95.19) * mm, "end": v(-34.92, -95.19) * mm});
            skLineSegment(sketch, "E78.MirrorCS", {"start": v(-34.92, -95.19) * mm, "end": v(-34.92, 95.19) * mm});
            skLineSegment(sketch, "E79.MirrorCS", {"start": v(-38.1, -95.19) * mm, "end": v(-38.1, 95.19) * mm});
            skLineSegment(sketch, "E80.MirrorCS", {"start": v(-38.1, 95.19) * mm, "end": v(-34.92, 95.19) * mm});
            skSolve(sketch);
        }
        {
            var Q0;
            Q0 = qSketchRegion(id + "F10", true);
            extrude(context, id + "F11", {"entities" : qUnion([Q0]), "operationType" : NewBodyOperationType.ADD, "depth" : 3.17 * mm, "offsetDistance" : 25.4 * mm});
        }
    });
